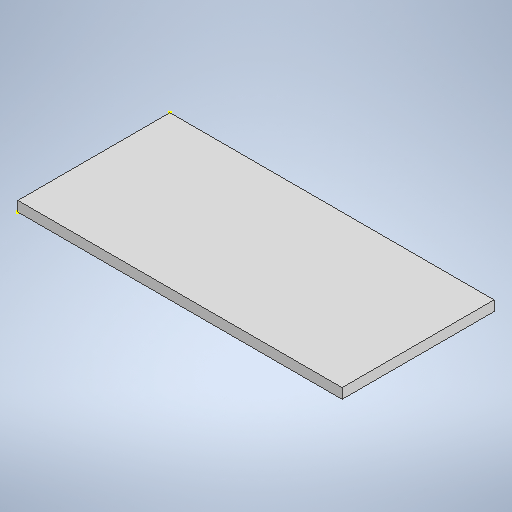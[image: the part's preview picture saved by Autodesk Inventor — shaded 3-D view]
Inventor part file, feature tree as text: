
AUTODESK INVENTOR PART (.ipt)
format: ipt  version: 2025.1 (Build 291241020, 241B)  size: 219,136 bytes
history: native  units: mm
features: sketch x3, extrude x1
ambient origin geometry x8: Origin, YZ Plane, XZ Plane, XY Plane, X Axis, Y Axis, Z Axis, Center Point
bodies: Solid1 (feature_tree)
feature tree (4):
  extrude  "Extrusion1"  Depth=2.0mm
  sketch  "Sketch2"  dims[d2=30.0mm d3=0.0mm]
  sketch  "Sketch3"  dims[d4=64.0mm d5=1.5mm]
  sketch  "Sketch1"  dims[d0=64.0mm d1=2.0mm]
